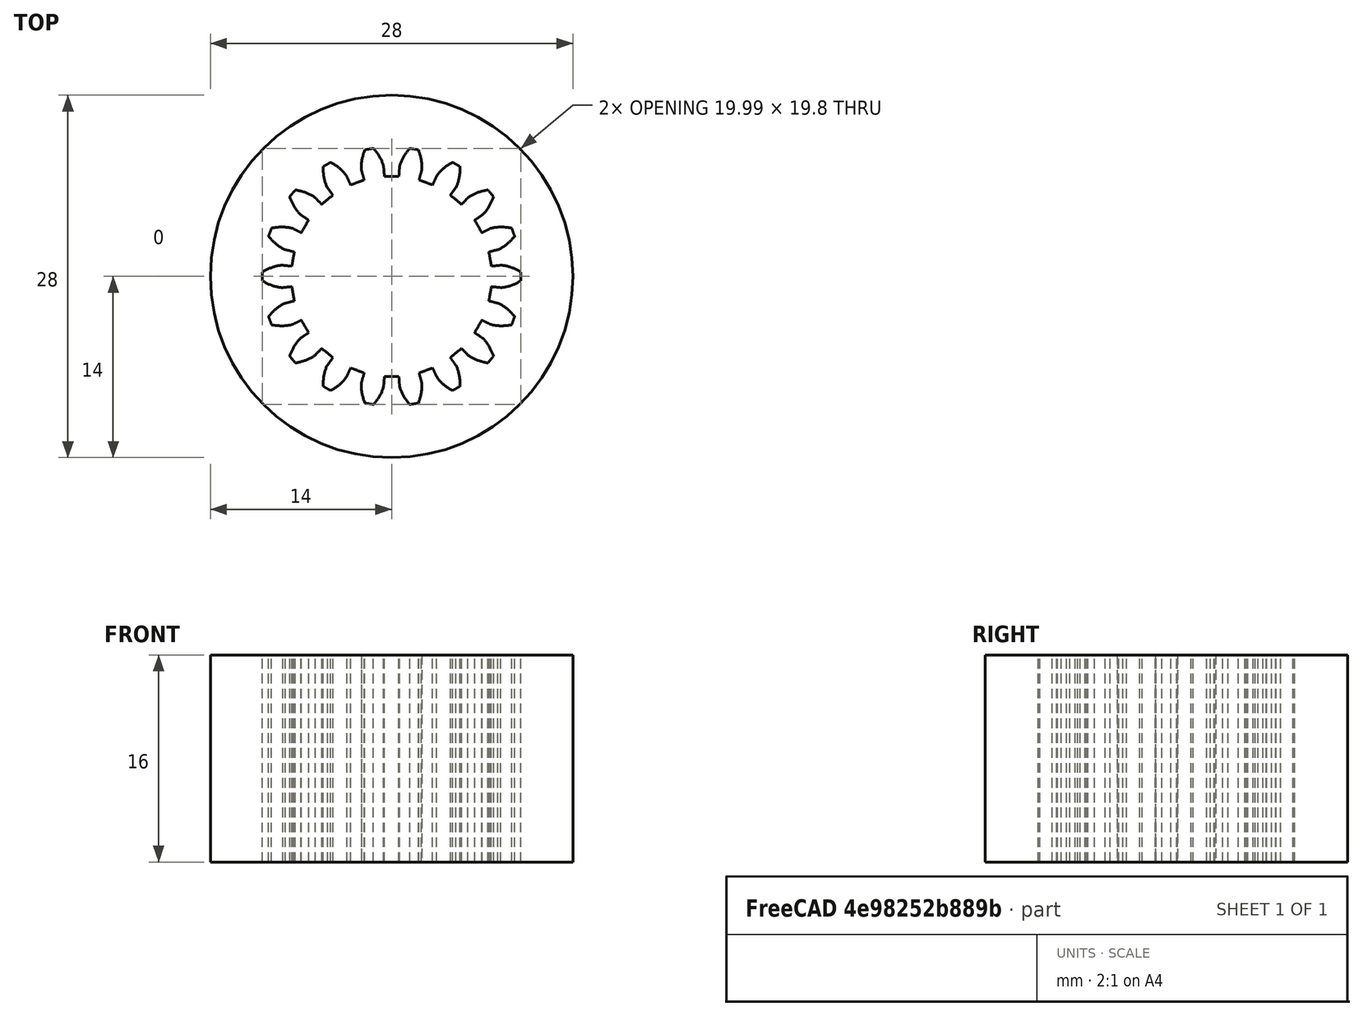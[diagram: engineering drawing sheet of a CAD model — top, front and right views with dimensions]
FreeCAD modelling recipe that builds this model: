
FCSTD DOCUMENT  (FreeCAD 0.19R24276 (Git))
Label: Gear_privod_perehodnik_to_GT2_gear_part_d28
License: All rights reserved
LicenseURL: http://en.wikipedia.org/wiki/All_rights_reserved
objects: Sketcher::SketchObject×1, PartDesign::FeaturePython×1, PartDesign::Pad×1, PartDesign::Body×1, Part::Cut×1
note: 6 computed .brp shape members not serialized (recipe doc carries the construction recipe); baked Part::Feature solids carry a one-line shape summary decoded from their .brp

FEATURE [Sketcher::SketchObject] Sketch  label="Sketch_d28"
  FullyConstrained = true
  MapMode = 5
  Support = -> [XY_Plane]
  sketch-geometry (1):
    g0: Circle CenterX=0 CenterY=0 CenterZ=0 NormalX=0 NormalY=0 NormalZ=1 AngleXU=0 Radius=14
  constraints (2):
    c: Coincident(g0,g-1)
    c: Diameter(g0) = 28
FEATURE [PartDesign::FeaturePython] involutegear  # WARN: FeaturePython — macro-defined, semantics opaque (R4)
  AttacherType = Attacher::AttachEngine3D
  backlash = 0
  beta = 0
  clearance = 0.25
  da = 20
  df = 15.5
  double_helix = false
  dw = 18
  head = 0
  height = 16
  module = 1
  numpoints = 6
  pressure_angle = 20
  properties_from_tool = false
  reversed_backlash = false
  shift = 0
  simple = false
  teeth = 18
  transverse_pitch = 3.14159
  undercut = false
  version = 0.0.3
FEATURE [PartDesign::Pad] Pad  label="Pad_h16"
  BaseFeature = -> involutegear
  Direction = (1,1,1)
  Length = 16
  Length2 = 100
  Profile = -> Sketch
  Type = 0
FEATURE [PartDesign::Body] Body
  Group = -> [Sketch,involutegear,Pad]
  Origin = -> Origin
  Tip = -> Pad
FEATURE [Part::Cut] Cut
  Base = -> Pad
  Tool = -> involutegear
